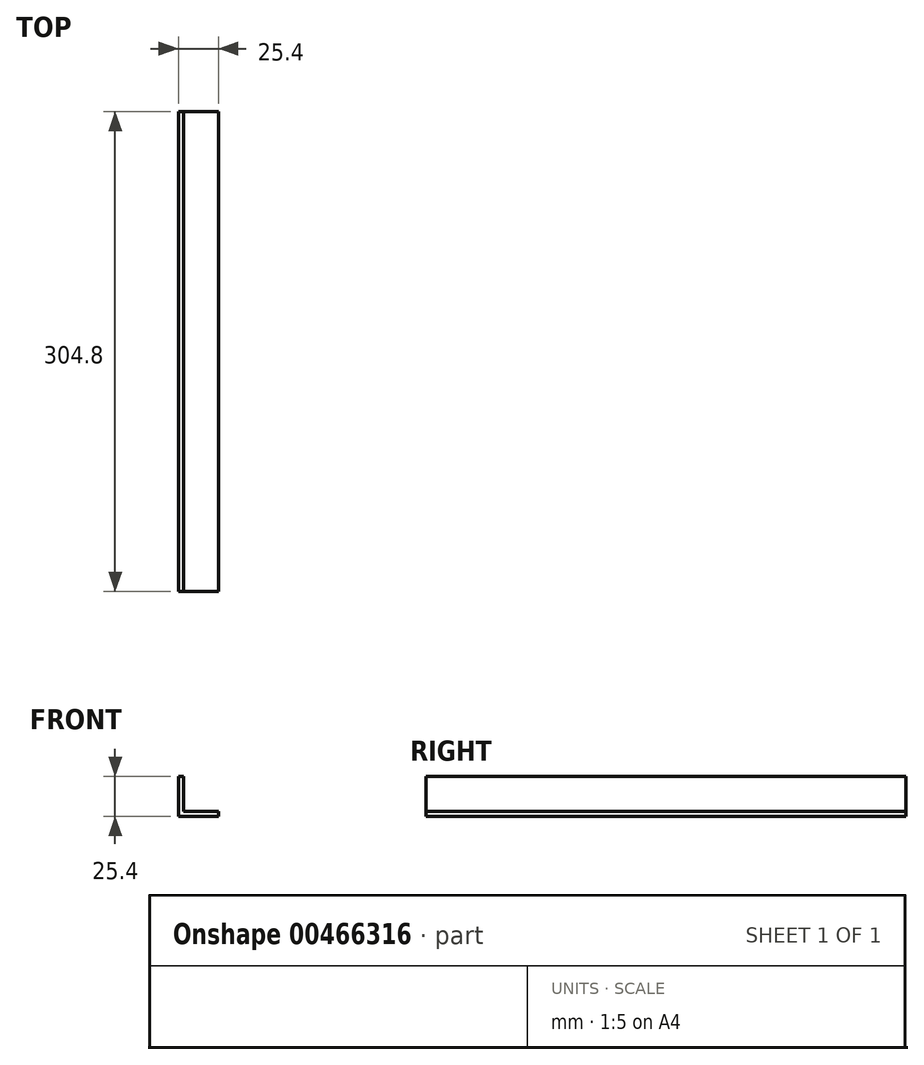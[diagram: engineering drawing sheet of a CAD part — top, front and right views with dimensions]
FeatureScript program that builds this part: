
annotation { "Feature Type Name" : "Feature", "Feature Type Description" : "" }
export const myFeature = defineFeature(function(context is Context, id is Id, definition is map)
    precondition{}
    {
        {
            var Q0;
            Q0=qCreatedBy(makeId("Front.planeOp"),FACE);
            var sketch = newSketch(context, id + "F0", { "sketchPlane" : qUnion([Q0])});
            skLineSegment(sketch, "E0", {"start": v(-25.4, 25.4) * mm, "end": v(-25.4, 0) * mm});
            skLineSegment(sketch, "E1", {"start": v(-25.4, 0) * mm, "end": v(0, 0) * mm});
            skLineSegment(sketch, "E2", {"start": v(-25.4, 25.4) * mm, "end": v(-22.23, 25.4) * mm});
            skLineSegment(sketch, "E3", {"start": v(0, 0) * mm, "end": v(0, 3.18) * mm});
            skLineSegment(sketch, "E4", {"start": v(-22.23, 25.4) * mm, "end": v(-22.23, 3.18) * mm});
            skLineSegment(sketch, "E5", {"start": v(0, 3.18) * mm, "end": v(-22.23, 3.18) * mm});
            skSolve(sketch);
        }
        {
            var Q0;
            Q0=qSketchRegion(id+"F0",true);
            extrude(context, id + "F1", {"entities" : qUnion([Q0]), "depth" : 304.8 * mm});
        }
    });
